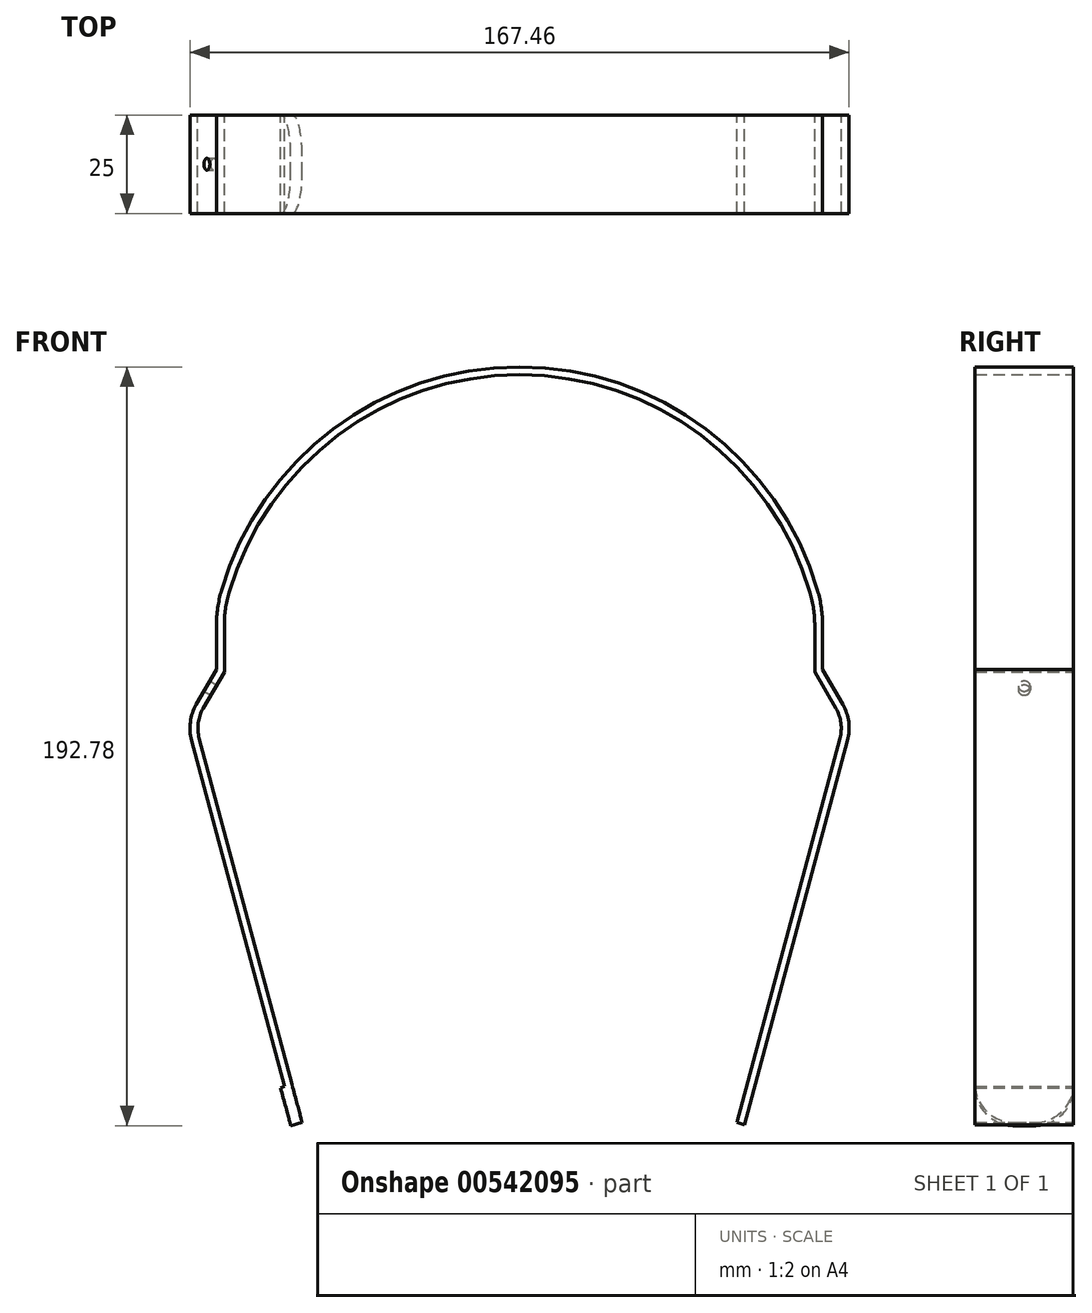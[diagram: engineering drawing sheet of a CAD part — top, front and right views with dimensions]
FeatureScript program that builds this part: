
annotation { "Feature Type Name" : "Feature", "Feature Type Description" : "" }
export const myFeature = defineFeature(function(context is Context, id is Id, definition is map)
    precondition{}
    {
        {
            var Q0;
            Q0=qCreatedBy(makeId("Front.planeOp"),FACE);
            var sketch = newSketch(context, id + "F0", { "sketchPlane" : qUnion([Q0])});
            skLineSegment(sketch, "E0", {"start": v(0, 60) * mm, "end": v(0, 0) * mm, "construction": true});
            skLineSegment(sketch, "E1", {"start": v(0, 0) * mm, "end": v(-75, 0) * mm, "construction": true});
            skArc(sketch, "E2", {"start": v(0, 60) * mm, "mid": v(-46.13, 44.62) * mm, "end": v(-73.8, 4.65) * mm});
            skPoint(sketch, "E2.startSnap0", {"position": v(-37.5, 0) * mm});
            skLineSegment(sketch, "E3", {"start": v(-75, -3.75) * mm, "end": v(-75, -15.45) * mm});
            skLineSegment(sketch, "E4", {"start": v(-75, -15.45) * mm, "end": v(-80.39, -24.78) * mm});
            skLineSegment(sketch, "E5", {"start": v(-81.39, -32.37) * mm, "end": v(-55.23, -130) * mm});
            skPoint(sketch, "E6.visualSharp", {"position": v(-75, 0) * mm});
            skArc(sketch, "E6.filletArc", {"start": v(-73.8, 4.65) * mm, "mid": v(-74.7, 0.5) * mm, "end": v(-75, -3.75) * mm});
            skPoint(sketch, "E7.visualSharp", {"position": v(-82.46, -28.37) * mm});
            skArc(sketch, "E7.filletArc", {"start": v(-80.39, -24.78) * mm, "mid": v(-81.64, -28.48) * mm, "end": v(-81.39, -32.37) * mm});
            skPoint(sketch, "E8.orphan", {"position": v(75, 0) * mm});
            skLineSegment(sketch, "E9.0", {"start": v(-83.32, -32.89) * mm, "end": v(-57.16, -130.52) * mm});
            skArc(sketch, "E9.1", {"start": v(-82.12, -23.78) * mm, "mid": v(-83.63, -28.22) * mm, "end": v(-83.32, -32.89) * mm});
            skArc(sketch, "E9.2", {"start": v(0, 62) * mm, "mid": v(-47.32, 46.22) * mm, "end": v(-75.72, 5.2) * mm});
            skArc(sketch, "E9.3", {"start": v(-75.72, 5.21) * mm, "mid": v(-76.68, 0.78) * mm, "end": v(-77, -3.75) * mm});
            skLineSegment(sketch, "E9.4", {"start": v(-77, -3.75) * mm, "end": v(-77, -14.91) * mm});
            skLineSegment(sketch, "E9.5", {"start": v(-77, -14.91) * mm, "end": v(-82.12, -23.78) * mm});
            skLineSegment(sketch, "E10", {"start": v(-57.16, -130.52) * mm, "end": v(-55.23, -130) * mm});
            skLineSegment(sketch, "E11", {"start": v(0, 62) * mm, "end": v(0, 60) * mm});
            skArc(sketch, "E12.MirrorCS", {"start": v(75.72, 5.21) * mm, "mid": v(76.68, 0.78) * mm, "end": v(77, -3.75) * mm});
            skArc(sketch, "E13.MirrorCS", {"start": v(82.12, -23.78) * mm, "mid": v(83.63, -28.22) * mm, "end": v(83.32, -32.89) * mm});
            skArc(sketch, "E14.MirrorCS", {"start": v(80.39, -24.78) * mm, "mid": v(81.64, -28.48) * mm, "end": v(81.39, -32.37) * mm});
            skArc(sketch, "E15.MirrorCS", {"start": v(73.8, 4.65) * mm, "mid": v(74.7, 0.5) * mm, "end": v(75, -3.75) * mm});
            skLineSegment(sketch, "E16.MirrorCS", {"start": v(75, -15.45) * mm, "end": v(80.39, -24.78) * mm});
            skLineSegment(sketch, "E17.MirrorCS", {"start": v(57.16, -130.52) * mm, "end": v(55.23, -130) * mm});
            skLineSegment(sketch, "E18.MirrorCS", {"start": v(77, -14.91) * mm, "end": v(82.12, -23.78) * mm});
            skLineSegment(sketch, "E19.MirrorCS", {"start": v(77, -3.75) * mm, "end": v(77, -14.91) * mm});
            skArc(sketch, "E20.MirrorCS", {"start": v(0, 62) * mm, "mid": v(47.32, 46.22) * mm, "end": v(75.72, 5.2) * mm});
            skLineSegment(sketch, "E21.MirrorCS", {"start": v(83.32, -32.89) * mm, "end": v(57.16, -130.52) * mm});
            skLineSegment(sketch, "E22.MirrorCS", {"start": v(81.39, -32.37) * mm, "end": v(55.23, -130) * mm});
            skLineSegment(sketch, "E23.MirrorCS", {"start": v(75, -3.75) * mm, "end": v(75, -15.45) * mm});
            skArc(sketch, "E24.MirrorCS", {"start": v(0, 60) * mm, "mid": v(46.13, 44.62) * mm, "end": v(73.8, 4.65) * mm});
            skPoint(sketch, "E25.MirrorP", {"position": v(82.46, -28.37) * mm});
            skLineSegment(sketch, "E26.MirrorCS", {"start": v(0, 0) * mm, "end": v(75, 0) * mm, "construction": true});
            skPoint(sketch, "E27.MirrorP", {"position": v(37.5, 0) * mm});
            skSolve(sketch);
        }
        {
            var Q0;
            Q0=makeQuery(id+"F0.imprint","IMPRINT",FACE,{"disambiguationData":[TD([[makeQuery(id+"F0.imprint","IMPRINT",EDGE,{"derivedFrom":sQuery(id+"F0.wireOp",EDGE,"E2")}),-1.0]])]});
            var Q1;
            Q1=makeQuery(id+"F0.imprint","IMPRINT",FACE,{"disambiguationData":[TD([[makeQuery(id+"F0.imprint","IMPRINT",EDGE,{"derivedFrom":sQuery(id+"F0.wireOp",EDGE,"E11")}),1.0]])]});
            extrude(context, id + "F1", {"entities" : qUnion([Q0, Q1]), "depth" : 25 * mm, "offsetDistance" : 25 * mm});
        }
        {
            var Q0;
            Q0=makeQuery(id+"F1.opExtrude","CAP_EDGE",EDGE,{"disambiguationData":[OSD([sQuery(id+"F0.wireOp",EDGE,"E10")])],"isStart":false});
            var Q1;
            Q1=makeQuery(id+"F1.opExtrude","CAP_EDGE",EDGE,{"disambiguationData":[OSD([sQuery(id+"F0.wireOp",EDGE,"E10")])],"isStart":true});
            fillet(context, id + "F2", {"entities" : qUnion([Q0, Q1]), "radius" : 10 * mm, "tangentPropagation" : true, "allowEdgeOverflow" : false});
        }
        {
            var Q0;
            Q0=makeQuery(id+"F1.opExtrude","SWEPT_FACE",FACE,{"disambiguationData":[OSD([sQuery(id+"F0.wireOp",EDGE,"E4")])]});
            var sketch = newSketch(context, id + "F3", { "sketchPlane" : qUnion([Q0])});
            skCircle(sketch, "E28", {"center": v(-12.5, -56.27) * mm, "radius": 1.5 * mm});
            skPoint(sketch, "E28.centerSnap0", {"position": v(0, -56.27) * mm});
            skPoint(sketch, "E28.centerSnap1", {"position": v(-12.5, -61.66) * mm});
            skSolve(sketch);
        }
        {
            var Q0;
            Q0=makeQuery(id+"F3.imprint","IMPRINT",FACE,{"disambiguationData":[TD([[makeQuery(id+"F3.imprint","IMPRINT",EDGE,{"derivedFrom":sQuery(id+"F3.wireOp",EDGE,"E28")}),1.0]])]});
            extrude(context, id + "F4", {"entities" : qUnion([Q0]), "operationType" : NewBodyOperationType.REMOVE, "oppositeDirection" : true, "depth" : 25 * mm, "offsetDistance" : 25 * mm});
        }
        {
            var Q0;
            Q0=makeQuery(id+"F1.opExtrude","SWEPT_FACE",FACE,{"disambiguationData":[OSD([sQuery(id+"F0.wireOp",EDGE,"E5")])]});
            var sketch = newSketch(context, id + "F5", { "sketchPlane" : qUnion([Q0])});
            skLineSegment(sketch, "E29", {"start": v(-25, -101.28) * mm, "end": v(0, -101.28) * mm});
            skLineSegment(sketch, "E30.0.0", {"start": v(-15, -111.28) * mm, "end": v(-10, -111.28) * mm});
            skArc(sketch, "E30.0.1", {"start": v(-10, -111.28) * mm, "mid": v(-2.93, -108.35) * mm, "end": v(0, -101.28) * mm});
            skLineSegment(sketch, "E30.0.2", {"start": v(0, -101.28) * mm, "end": v(0, -10.2) * mm});
            skLineSegment(sketch, "E30.0.3", {"start": v(0, -10.2) * mm, "end": v(-25, -10.2) * mm});
            skLineSegment(sketch, "E30.0.4", {"start": v(-25, -10.2) * mm, "end": v(-25, -101.28) * mm});
            skArc(sketch, "E30.0.5", {"start": v(-25, -101.28) * mm, "mid": v(-22.07, -108.35) * mm, "end": v(-15, -111.28) * mm});
            skArc(sketch, "E31.0.0", {"start": v(0, -101.28) * mm, "mid": v(-2.93, -108.35) * mm, "end": v(-10, -111.28) * mm});
            skArc(sketch, "E31.0.2", {"start": v(0, -101.28) * mm, "mid": v(-2.93, -108.35) * mm, "end": v(-10, -111.28) * mm});
            skSolve(sketch);
        }
        {
            var Q0;
            Q0=makeQuery(id+"F5.imprint","IMPRINT",FACE,{"disambiguationData":[TD([[makeQuery(id+"F5.imprint","IMPRINT",EDGE,{"derivedFrom":sQuery(id+"F5.wireOp",EDGE,"E29")}),-1.0]])]});
            extrude(context, id + "F6", {"entities" : qUnion([Q0]), "operationType" : NewBodyOperationType.ADD, "oppositeDirection" : true, "depth" : 3 * mm, "offsetDistance" : 25 * mm});
        }
    });
